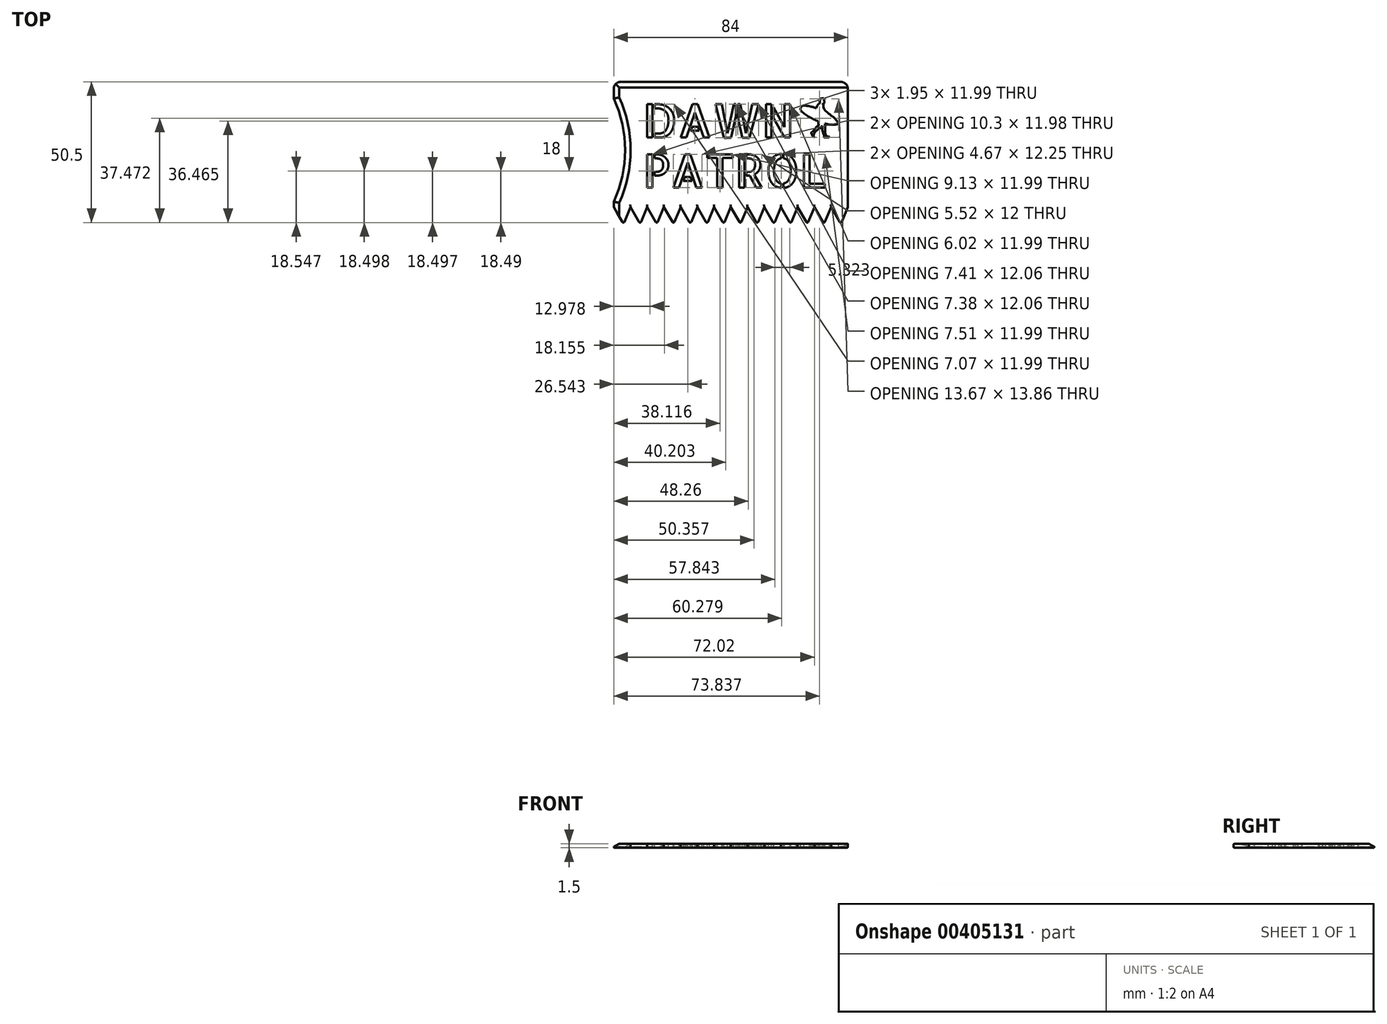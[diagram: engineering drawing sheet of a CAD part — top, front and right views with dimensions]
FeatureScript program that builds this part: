
annotation { "Feature Type Name" : "Feature", "Feature Type Description" : "" }
export const myFeature = defineFeature(function(context is Context, id is Id, definition is map)
    precondition{}
    {
        {
            assignVariable(context, id + "F0", {"name" : "t", "anyValue" : 1.5});
        }
        {
            var Q0;
            Q0=qCreatedBy(makeId("Top.planeOp"),FACE);
            var sketch = newSketch(context, id + "F1", { "sketchPlane" : qUnion([Q0])});
            skLineSegment(sketch, "E0.bottom", {"start": v(84, 51) * mm, "end": v(0, 51) * mm});
            skLineSegment(sketch, "E0.top", {"start": v(81.5, 0) * mm, "end": v(3.5, 0) * mm, "construction": true});
            skLineSegment(sketch, "E0.left", {"start": v(84, 51) * mm, "end": v(84, 6) * mm});
            skLineSegment(sketch, "E0.right", {"start": v(0, 51) * mm, "end": v(0, 6) * mm, "construction": true});
            skLineSegment(sketch, "E1", {"start": v(84, 6) * mm, "end": v(0, 6) * mm, "construction": true});
            skLineSegment(sketch, "E2", {"start": v(84, 6) * mm, "end": v(81.5, 0) * mm});
            skLineSegment(sketch, "E3", {"start": v(81.5, 0) * mm, "end": v(78, 6) * mm});
            skLineSegment(sketch, "E4.1.0.0", {"start": v(78, 6) * mm, "end": v(75.5, 0) * mm});
            skLineSegment(sketch, "E4.1.0.1", {"start": v(75.5, 0) * mm, "end": v(72, 6) * mm});
            skLineSegment(sketch, "E4.2.0.0", {"start": v(72, 6) * mm, "end": v(69.5, 0) * mm});
            skLineSegment(sketch, "E4.2.0.1", {"start": v(69.5, 0) * mm, "end": v(66, 6) * mm});
            skLineSegment(sketch, "E4.3.0.0", {"start": v(66, 6) * mm, "end": v(63.5, 0) * mm});
            skLineSegment(sketch, "E4.3.0.1", {"start": v(63.5, 0) * mm, "end": v(60, 6) * mm});
            skLineSegment(sketch, "E4.4.0.0", {"start": v(60, 6) * mm, "end": v(57.5, 0) * mm});
            skLineSegment(sketch, "E4.4.0.1", {"start": v(57.5, 0) * mm, "end": v(54, 6) * mm});
            skLineSegment(sketch, "E4.5.0.0", {"start": v(54, 6) * mm, "end": v(51.5, 0) * mm});
            skLineSegment(sketch, "E4.5.0.1", {"start": v(51.5, 0) * mm, "end": v(48, 6) * mm});
            skLineSegment(sketch, "E4.6.0.0", {"start": v(48, 6) * mm, "end": v(45.5, 0) * mm});
            skLineSegment(sketch, "E4.6.0.1", {"start": v(45.5, 0) * mm, "end": v(42, 6) * mm});
            skLineSegment(sketch, "E4.7.0.0", {"start": v(42, 6) * mm, "end": v(39.5, 0) * mm});
            skLineSegment(sketch, "E4.7.0.1", {"start": v(39.5, 0) * mm, "end": v(36, 6) * mm});
            skLineSegment(sketch, "E4.8.0.0", {"start": v(36, 6) * mm, "end": v(33.5, 0) * mm});
            skLineSegment(sketch, "E4.8.0.1", {"start": v(33.5, 0) * mm, "end": v(30, 6) * mm});
            skLineSegment(sketch, "E4.9.0.0", {"start": v(30, 6) * mm, "end": v(27.5, 0) * mm});
            skLineSegment(sketch, "E4.9.0.1", {"start": v(27.5, 0) * mm, "end": v(24, 6) * mm});
            skLineSegment(sketch, "E4.10.0.0", {"start": v(24, 6) * mm, "end": v(21.5, 0) * mm});
            skLineSegment(sketch, "E4.10.0.1", {"start": v(21.5, 0) * mm, "end": v(18, 6) * mm});
            skLineSegment(sketch, "E4.11.0.0", {"start": v(18, 6) * mm, "end": v(15.5, 0) * mm});
            skLineSegment(sketch, "E4.11.0.1", {"start": v(15.5, 0) * mm, "end": v(12, 6) * mm});
            skLineSegment(sketch, "E4.12.0.0", {"start": v(12, 6) * mm, "end": v(9.5, 0) * mm});
            skLineSegment(sketch, "E4.12.0.1", {"start": v(9.5, 0) * mm, "end": v(6, 6) * mm});
            skLineSegment(sketch, "E4.13.0.0", {"start": v(6, 6) * mm, "end": v(3.5, 0) * mm});
            skLineSegment(sketch, "E4.13.0.1", {"start": v(3.5, 0) * mm, "end": v(0, 6) * mm});
            skLineSegment(sketch, "E4.direction1", {"start": v(84, 6) * mm, "end": v(78, 6) * mm, "construction": true});
            skLineSegment(sketch, "E5", {"start": v(0, 6) * mm, "end": v(0, 8) * mm});
            skArc(sketch, "E6", {"start": v(0, 8) * mm, "mid": v(4.07, 26.5) * mm, "end": v(0, 45) * mm});
            skLineSegment(sketch, "E7", {"start": v(0, 45) * mm, "end": v(0, 51) * mm});
            skLineSegment(sketch, "E8", {"start": v(0, 6) * mm, "end": v(0, 0) * mm, "construction": true});
            skSolve(sketch);
        }
        {
            var Q0;
            Q0=qSketchRegion(id+"F1",true);
            extrude(context, id + "F2", {"entities" : qUnion([Q0]), "depth" : (getVariable(context, 't')) * mm});
        }
        {
            var Q0;
            Q0=makeQuery(id+"F2.opExtrude","CAP_EDGE",EDGE,{"disambiguationData":[OSD([sQuery(id+"F1.wireOp",EDGE,"E5")])],"isStart":false});
            var Q1;
            Q1=makeQuery(id+"F2.opExtrude","CAP_EDGE",EDGE,{"disambiguationData":[OSD([sQuery(id+"F1.wireOp",EDGE,"E6")])],"isStart":false});
            var Q2;
            Q2=makeQuery(id+"F2.opExtrude","CAP_EDGE",EDGE,{"disambiguationData":[OSD([sQuery(id+"F1.wireOp",EDGE,"E0.bottom")])],"isStart":false});
            var Q3;
            Q3=makeQuery(id+"F2.opExtrude","CAP_EDGE",EDGE,{"disambiguationData":[OSD([sQuery(id+"F1.wireOp",EDGE,"E7")])],"isStart":false});
            chamfer(context, id + "F3", {"entities" : qUnion([Q0, Q1, Q2, Q3]), "chamferType" : ChamferType.TWO_OFFSETS, "width1" : (getVariable(context, 't') * 2.2 / 3) * mm, "oppositeDirection" : false, "width2" : (getVariable(context, 't') * 4 / 3) * mm, "tangentPropagation" : true});
        }
        {
            var Q0;
            Q0=makeQuery(id+"F2.opExtrude","SWEPT_EDGE",EDGE,{"disambiguationData":[OSD([sQuery(id+"F1.wireOp",EDGE,"E0.bottom"),sQuery(id+"F1.wireOp",EDGE,"E7")])]});
            var Q1;
            Q1=makeQuery(id+"F2.opExtrude","SWEPT_EDGE",EDGE,{"disambiguationData":[OSD([sQuery(id+"F1.wireOp",EDGE,"E0.bottom"),sQuery(id+"F1.wireOp",EDGE,"E0.left")])]});
            fillet(context, id + "F4", {"entities" : qUnion([Q0, Q1]), "radius" : 2.5 * mm, "tangentPropagation" : true, "allowEdgeOverflow" : false});
        }
        {
            var Q0;
            Q0=makeQuery(id+"F2.opExtrude","CAP_FACE",FACE,{"disambiguationData":[OSD([sQuery(id+"F1.wireOp",EDGE,"E0.bottom"),sQuery(id+"F1.wireOp",EDGE,"E0.left"),sQuery(id+"F1.wireOp",EDGE,"E2"),sQuery(id+"F1.wireOp",EDGE,"E3"),sQuery(id+"F1.wireOp",EDGE,"E4.1.0.0"),sQuery(id+"F1.wireOp",EDGE,"E4.1.0.1"),sQuery(id+"F1.wireOp",EDGE,"E4.2.0.0"),sQuery(id+"F1.wireOp",EDGE,"E4.2.0.1"),sQuery(id+"F1.wireOp",EDGE,"E4.3.0.0"),sQuery(id+"F1.wireOp",EDGE,"E4.3.0.1"),sQuery(id+"F1.wireOp",EDGE,"E4.4.0.0"),sQuery(id+"F1.wireOp",EDGE,"E4.4.0.1"),sQuery(id+"F1.wireOp",EDGE,"E4.5.0.0"),sQuery(id+"F1.wireOp",EDGE,"E4.5.0.1"),sQuery(id+"F1.wireOp",EDGE,"E4.6.0.0"),sQuery(id+"F1.wireOp",EDGE,"E4.6.0.1"),sQuery(id+"F1.wireOp",EDGE,"E4.7.0.0"),sQuery(id+"F1.wireOp",EDGE,"E4.7.0.1"),sQuery(id+"F1.wireOp",EDGE,"E4.8.0.0"),sQuery(id+"F1.wireOp",EDGE,"E4.8.0.1"),sQuery(id+"F1.wireOp",EDGE,"E4.9.0.0"),sQuery(id+"F1.wireOp",EDGE,"E4.9.0.1"),sQuery(id+"F1.wireOp",EDGE,"E4.10.0.0"),sQuery(id+"F1.wireOp",EDGE,"E4.10.0.1"),sQuery(id+"F1.wireOp",EDGE,"E4.11.0.0"),sQuery(id+"F1.wireOp",EDGE,"E4.11.0.1"),sQuery(id+"F1.wireOp",EDGE,"E4.12.0.0"),sQuery(id+"F1.wireOp",EDGE,"E4.12.0.1"),sQuery(id+"F1.wireOp",EDGE,"E4.13.0.0"),sQuery(id+"F1.wireOp",EDGE,"E4.13.0.1"),sQuery(id+"F1.wireOp",EDGE,"E5"),sQuery(id+"F1.wireOp",EDGE,"E6"),sQuery(id+"F1.wireOp",EDGE,"E7")])],"isStart":false});
            var sketch = newSketch(context, id + "F5", { "sketchPlane" : qUnion([Q0])});
            skLineSegment(sketch, "E9.0", {"start": v(81.9, 6.42) * mm, "end": v(81.9, 46.9) * mm});
            skLineSegment(sketch, "E9.1", {"start": v(81.19, 4.7) * mm, "end": v(81.9, 6.42) * mm});
            skLineSegment(sketch, "E9.2", {"start": v(77.69, 10.7) * mm, "end": v(81.19, 4.7) * mm});
            skLineSegment(sketch, "E9.3", {"start": v(75.19, 4.7) * mm, "end": v(77.69, 10.7) * mm});
            skLineSegment(sketch, "E9.4", {"start": v(71.69, 10.7) * mm, "end": v(75.19, 4.7) * mm});
            skLineSegment(sketch, "E9.5", {"start": v(69.19, 4.7) * mm, "end": v(71.69, 10.7) * mm});
            skLineSegment(sketch, "E9.6", {"start": v(65.69, 10.7) * mm, "end": v(69.19, 4.7) * mm});
            skLineSegment(sketch, "E9.7", {"start": v(81.9, 46.9) * mm, "end": v(3.64, 46.9) * mm});
            skArc(sketch, "E9.8", {"start": v(3.64, 46.9) * mm, "mid": v(8.1, 29.09) * mm, "end": v(5.57, 10.9) * mm});
            skLineSegment(sketch, "E9.9", {"start": v(5.57, 10.9) * mm, "end": v(9.19, 4.7) * mm});
            skLineSegment(sketch, "E9.10", {"start": v(9.19, 4.7) * mm, "end": v(11.69, 10.7) * mm});
            skLineSegment(sketch, "E9.11", {"start": v(11.69, 10.7) * mm, "end": v(15.19, 4.7) * mm});
            skLineSegment(sketch, "E9.12", {"start": v(15.19, 4.7) * mm, "end": v(17.69, 10.7) * mm});
            skLineSegment(sketch, "E9.13", {"start": v(17.69, 10.7) * mm, "end": v(21.19, 4.7) * mm});
            skLineSegment(sketch, "E9.14", {"start": v(21.19, 4.7) * mm, "end": v(23.69, 10.7) * mm});
            skLineSegment(sketch, "E9.15", {"start": v(23.69, 10.7) * mm, "end": v(27.19, 4.7) * mm});
            skLineSegment(sketch, "E9.16", {"start": v(27.19, 4.7) * mm, "end": v(29.69, 10.7) * mm});
            skLineSegment(sketch, "E9.17", {"start": v(29.69, 10.7) * mm, "end": v(33.19, 4.7) * mm});
            skLineSegment(sketch, "E9.18", {"start": v(33.19, 4.7) * mm, "end": v(35.69, 10.7) * mm});
            skLineSegment(sketch, "E9.19", {"start": v(35.69, 10.7) * mm, "end": v(39.19, 4.7) * mm});
            skLineSegment(sketch, "E9.20", {"start": v(39.19, 4.7) * mm, "end": v(41.69, 10.7) * mm});
            skLineSegment(sketch, "E9.21", {"start": v(41.69, 10.7) * mm, "end": v(45.19, 4.7) * mm});
            skLineSegment(sketch, "E9.22", {"start": v(45.19, 4.7) * mm, "end": v(47.69, 10.7) * mm});
            skLineSegment(sketch, "E9.23", {"start": v(47.69, 10.7) * mm, "end": v(51.19, 4.7) * mm});
            skLineSegment(sketch, "E9.24", {"start": v(51.19, 4.7) * mm, "end": v(53.69, 10.7) * mm});
            skLineSegment(sketch, "E9.25", {"start": v(53.69, 10.7) * mm, "end": v(57.19, 4.7) * mm});
            skLineSegment(sketch, "E9.26", {"start": v(57.19, 4.7) * mm, "end": v(59.69, 10.7) * mm});
            skLineSegment(sketch, "E9.27", {"start": v(59.69, 10.7) * mm, "end": v(63.19, 4.7) * mm});
            skLineSegment(sketch, "E9.28", {"start": v(63.19, 4.7) * mm, "end": v(65.69, 10.7) * mm});
            skSolve(sketch);
        }
        {
            var Q0;
            Q0=makeQuery(id+"F2.opExtrude","CAP_FACE",FACE,{"disambiguationData":[OSD([sQuery(id+"F1.wireOp",EDGE,"E0.bottom"),sQuery(id+"F1.wireOp",EDGE,"E0.left"),sQuery(id+"F1.wireOp",EDGE,"E2"),sQuery(id+"F1.wireOp",EDGE,"E3"),sQuery(id+"F1.wireOp",EDGE,"E4.1.0.0"),sQuery(id+"F1.wireOp",EDGE,"E4.1.0.1"),sQuery(id+"F1.wireOp",EDGE,"E4.2.0.0"),sQuery(id+"F1.wireOp",EDGE,"E4.2.0.1"),sQuery(id+"F1.wireOp",EDGE,"E4.3.0.0"),sQuery(id+"F1.wireOp",EDGE,"E4.3.0.1"),sQuery(id+"F1.wireOp",EDGE,"E4.4.0.0"),sQuery(id+"F1.wireOp",EDGE,"E4.4.0.1"),sQuery(id+"F1.wireOp",EDGE,"E4.5.0.0"),sQuery(id+"F1.wireOp",EDGE,"E4.5.0.1"),sQuery(id+"F1.wireOp",EDGE,"E4.6.0.0"),sQuery(id+"F1.wireOp",EDGE,"E4.6.0.1"),sQuery(id+"F1.wireOp",EDGE,"E4.7.0.0"),sQuery(id+"F1.wireOp",EDGE,"E4.7.0.1"),sQuery(id+"F1.wireOp",EDGE,"E4.8.0.0"),sQuery(id+"F1.wireOp",EDGE,"E4.8.0.1"),sQuery(id+"F1.wireOp",EDGE,"E4.9.0.0"),sQuery(id+"F1.wireOp",EDGE,"E4.9.0.1"),sQuery(id+"F1.wireOp",EDGE,"E4.10.0.0"),sQuery(id+"F1.wireOp",EDGE,"E4.10.0.1"),sQuery(id+"F1.wireOp",EDGE,"E4.11.0.0"),sQuery(id+"F1.wireOp",EDGE,"E4.11.0.1"),sQuery(id+"F1.wireOp",EDGE,"E4.12.0.0"),sQuery(id+"F1.wireOp",EDGE,"E4.12.0.1"),sQuery(id+"F1.wireOp",EDGE,"E4.13.0.0"),sQuery(id+"F1.wireOp",EDGE,"E4.13.0.1"),sQuery(id+"F1.wireOp",EDGE,"E5"),sQuery(id+"F1.wireOp",EDGE,"E6"),sQuery(id+"F1.wireOp",EDGE,"E7")])],"isStart":true});
            var Q1;
            Q1=makeQuery(id+"F2.opExtrude","CAP_EDGE",EDGE,{"disambiguationData":[OSD([sQuery(id+"F1.wireOp",EDGE,"E4.13.0.1")])],"isStart":false});
            var Q2;
            Q2=makeQuery(id+"F2.opExtrude","CAP_EDGE",EDGE,{"disambiguationData":[OSD([sQuery(id+"F1.wireOp",EDGE,"E4.13.0.0")])],"isStart":false});
            var Q3;
            Q3=makeQuery(id+"F2.opExtrude","SWEPT_EDGE",EDGE,{"disambiguationData":[OSD([sQuery(id+"F1.wireOp",EDGE,"E4.13.0.0"),sQuery(id+"F1.wireOp",EDGE,"E4.13.0.1")])]});
            var Q4;
            Q4=makeQuery(id+"F2.opExtrude","CAP_EDGE",EDGE,{"disambiguationData":[OSD([sQuery(id+"F1.wireOp",EDGE,"E4.12.0.1")])],"isStart":false});
            var Q5;
            Q5=makeQuery(id+"F2.opExtrude","SWEPT_EDGE",EDGE,{"disambiguationData":[OSD([sQuery(id+"F1.wireOp",EDGE,"E4.12.0.0"),sQuery(id+"F1.wireOp",EDGE,"E4.12.0.1")])]});
            var Q6;
            Q6=makeQuery(id+"F2.opExtrude","CAP_EDGE",EDGE,{"disambiguationData":[OSD([sQuery(id+"F1.wireOp",EDGE,"E4.12.0.0")])],"isStart":false});
            var Q7;
            Q7=makeQuery(id+"F2.opExtrude","CAP_EDGE",EDGE,{"disambiguationData":[OSD([sQuery(id+"F1.wireOp",EDGE,"E4.11.0.1")])],"isStart":false});
            var Q8;
            Q8=makeQuery(id+"F2.opExtrude","SWEPT_EDGE",EDGE,{"disambiguationData":[OSD([sQuery(id+"F1.wireOp",EDGE,"E4.11.0.0"),sQuery(id+"F1.wireOp",EDGE,"E4.11.0.1")])]});
            var Q9;
            Q9=makeQuery(id+"F2.opExtrude","CAP_EDGE",EDGE,{"disambiguationData":[OSD([sQuery(id+"F1.wireOp",EDGE,"E4.11.0.0")])],"isStart":false});
            var Q10;
            Q10=makeQuery(id+"F2.opExtrude","CAP_EDGE",EDGE,{"disambiguationData":[OSD([sQuery(id+"F1.wireOp",EDGE,"E4.10.0.1")])],"isStart":false});
            var Q11;
            Q11=makeQuery(id+"F2.opExtrude","CAP_EDGE",EDGE,{"disambiguationData":[OSD([sQuery(id+"F1.wireOp",EDGE,"E4.10.0.0")])],"isStart":false});
            var Q12;
            Q12=makeQuery(id+"F2.opExtrude","CAP_EDGE",EDGE,{"disambiguationData":[OSD([sQuery(id+"F1.wireOp",EDGE,"E4.9.0.1")])],"isStart":false});
            var Q13;
            Q13=makeQuery(id+"F2.opExtrude","CAP_EDGE",EDGE,{"disambiguationData":[OSD([sQuery(id+"F1.wireOp",EDGE,"E4.9.0.0")])],"isStart":false});
            var Q14;
            Q14=makeQuery(id+"F2.opExtrude","CAP_EDGE",EDGE,{"disambiguationData":[OSD([sQuery(id+"F1.wireOp",EDGE,"E4.8.0.1")])],"isStart":false});
            var Q15;
            Q15=makeQuery(id+"F2.opExtrude","CAP_EDGE",EDGE,{"disambiguationData":[OSD([sQuery(id+"F1.wireOp",EDGE,"E4.8.0.0")])],"isStart":false});
            var Q16;
            Q16=makeQuery(id+"F2.opExtrude","CAP_EDGE",EDGE,{"disambiguationData":[OSD([sQuery(id+"F1.wireOp",EDGE,"E4.7.0.1")])],"isStart":false});
            var Q17;
            Q17=makeQuery(id+"F2.opExtrude","CAP_EDGE",EDGE,{"disambiguationData":[OSD([sQuery(id+"F1.wireOp",EDGE,"E4.7.0.0")])],"isStart":false});
            var Q18;
            Q18=makeQuery(id+"F2.opExtrude","CAP_EDGE",EDGE,{"disambiguationData":[OSD([sQuery(id+"F1.wireOp",EDGE,"E4.6.0.1")])],"isStart":false});
            var Q19;
            Q19=makeQuery(id+"F2.opExtrude","CAP_EDGE",EDGE,{"disambiguationData":[OSD([sQuery(id+"F1.wireOp",EDGE,"E4.6.0.0")])],"isStart":false});
            var Q20;
            Q20=makeQuery(id+"F2.opExtrude","CAP_EDGE",EDGE,{"disambiguationData":[OSD([sQuery(id+"F1.wireOp",EDGE,"E4.5.0.1")])],"isStart":false});
            var Q21;
            Q21=makeQuery(id+"F2.opExtrude","CAP_EDGE",EDGE,{"disambiguationData":[OSD([sQuery(id+"F1.wireOp",EDGE,"E4.5.0.0")])],"isStart":false});
            var Q22;
            Q22=makeQuery(id+"F2.opExtrude","CAP_EDGE",EDGE,{"disambiguationData":[OSD([sQuery(id+"F1.wireOp",EDGE,"E4.4.0.1")])],"isStart":false});
            var Q23;
            Q23=makeQuery(id+"F2.opExtrude","CAP_EDGE",EDGE,{"disambiguationData":[OSD([sQuery(id+"F1.wireOp",EDGE,"E4.4.0.0")])],"isStart":false});
            var Q24;
            Q24=makeQuery(id+"F2.opExtrude","CAP_EDGE",EDGE,{"disambiguationData":[OSD([sQuery(id+"F1.wireOp",EDGE,"E4.3.0.1")])],"isStart":false});
            var Q25;
            Q25=makeQuery(id+"F2.opExtrude","CAP_EDGE",EDGE,{"disambiguationData":[OSD([sQuery(id+"F1.wireOp",EDGE,"E4.3.0.0")])],"isStart":false});
            var Q26;
            Q26=makeQuery(id+"F2.opExtrude","CAP_EDGE",EDGE,{"disambiguationData":[OSD([sQuery(id+"F1.wireOp",EDGE,"E4.2.0.1")])],"isStart":false});
            var Q27;
            Q27=makeQuery(id+"F2.opExtrude","CAP_EDGE",EDGE,{"disambiguationData":[OSD([sQuery(id+"F1.wireOp",EDGE,"E4.2.0.0")])],"isStart":false});
            var Q28;
            Q28=makeQuery(id+"F2.opExtrude","CAP_EDGE",EDGE,{"disambiguationData":[OSD([sQuery(id+"F1.wireOp",EDGE,"E4.1.0.1")])],"isStart":false});
            var Q29;
            Q29=makeQuery(id+"F2.opExtrude","CAP_EDGE",EDGE,{"disambiguationData":[OSD([sQuery(id+"F1.wireOp",EDGE,"E4.1.0.0")])],"isStart":false});
            var Q30;
            Q30=makeQuery(id+"F2.opExtrude","CAP_EDGE",EDGE,{"disambiguationData":[OSD([sQuery(id+"F1.wireOp",EDGE,"E3")])],"isStart":false});
            var Q31;
            Q31=makeQuery(id+"F2.opExtrude","SWEPT_EDGE",EDGE,{"disambiguationData":[OSD([sQuery(id+"F1.wireOp",EDGE,"E2"),sQuery(id+"F1.wireOp",EDGE,"E3")])]});
            var Q32;
            Q32=makeQuery(id+"F2.opExtrude","CAP_EDGE",EDGE,{"disambiguationData":[OSD([sQuery(id+"F1.wireOp",EDGE,"E2")])],"isStart":false});
            var Q33;
            Q33=makeQuery(id+"F2.opExtrude","SWEPT_EDGE",EDGE,{"disambiguationData":[OSD([sQuery(id+"F1.wireOp",EDGE,"E4.1.0.0"),sQuery(id+"F1.wireOp",EDGE,"E4.1.0.1")])]});
            var Q34;
            Q34=makeQuery(id+"F2.opExtrude","SWEPT_EDGE",EDGE,{"disambiguationData":[OSD([sQuery(id+"F1.wireOp",EDGE,"E4.2.0.0"),sQuery(id+"F1.wireOp",EDGE,"E4.2.0.1")])]});
            var Q35;
            Q35=makeQuery(id+"F2.opExtrude","SWEPT_EDGE",EDGE,{"disambiguationData":[OSD([sQuery(id+"F1.wireOp",EDGE,"E4.3.0.0"),sQuery(id+"F1.wireOp",EDGE,"E4.3.0.1")])]});
            var Q36;
            Q36=makeQuery(id+"F2.opExtrude","SWEPT_EDGE",EDGE,{"disambiguationData":[OSD([sQuery(id+"F1.wireOp",EDGE,"E4.4.0.0"),sQuery(id+"F1.wireOp",EDGE,"E4.4.0.1")])]});
            var Q37;
            Q37=makeQuery(id+"F2.opExtrude","SWEPT_EDGE",EDGE,{"disambiguationData":[OSD([sQuery(id+"F1.wireOp",EDGE,"E4.5.0.0"),sQuery(id+"F1.wireOp",EDGE,"E4.5.0.1")])]});
            var Q38;
            Q38=makeQuery(id+"F2.opExtrude","SWEPT_EDGE",EDGE,{"disambiguationData":[OSD([sQuery(id+"F1.wireOp",EDGE,"E4.6.0.0"),sQuery(id+"F1.wireOp",EDGE,"E4.6.0.1")])]});
            var Q39;
            Q39=makeQuery(id+"F2.opExtrude","SWEPT_EDGE",EDGE,{"disambiguationData":[OSD([sQuery(id+"F1.wireOp",EDGE,"E4.7.0.0"),sQuery(id+"F1.wireOp",EDGE,"E4.7.0.1")])]});
            var Q40;
            Q40=makeQuery(id+"F2.opExtrude","SWEPT_EDGE",EDGE,{"disambiguationData":[OSD([sQuery(id+"F1.wireOp",EDGE,"E4.8.0.0"),sQuery(id+"F1.wireOp",EDGE,"E4.8.0.1")])]});
            var Q41;
            Q41=makeQuery(id+"F2.opExtrude","SWEPT_EDGE",EDGE,{"disambiguationData":[OSD([sQuery(id+"F1.wireOp",EDGE,"E4.9.0.0"),sQuery(id+"F1.wireOp",EDGE,"E4.9.0.1")])]});
            var Q42;
            Q42=makeQuery(id+"F2.opExtrude","SWEPT_EDGE",EDGE,{"disambiguationData":[OSD([sQuery(id+"F1.wireOp",EDGE,"E4.10.0.0"),sQuery(id+"F1.wireOp",EDGE,"E4.10.0.1")])]});
            fillet(context, id + "F6", {"entities" : qUnion([Q0, Q1, Q2, Q3, Q4, Q5, Q6, Q7, Q8, Q9, Q10, Q11, Q12, Q13, Q14, Q15, Q16, Q17, Q18, Q19, Q20, Q21, Q22, Q23, Q24, Q25, Q26, Q27, Q28, Q29, Q30, Q31, Q32, Q33, Q34, Q35, Q36, Q37, Q38, Q39, Q40, Q41, Q42]), "radius" : .4 * mm, "tangentPropagation" : true, "allowEdgeOverflow" : false});
        }
        {
            var Q0;
            Q0=makeQuery(id+"F2.opExtrude","CAP_FACE",FACE,{"disambiguationData":[OSD([sQuery(id+"F1.wireOp",EDGE,"E0.bottom"),sQuery(id+"F1.wireOp",EDGE,"E0.left"),sQuery(id+"F1.wireOp",EDGE,"E2"),sQuery(id+"F1.wireOp",EDGE,"E3"),sQuery(id+"F1.wireOp",EDGE,"E4.1.0.0"),sQuery(id+"F1.wireOp",EDGE,"E4.1.0.1"),sQuery(id+"F1.wireOp",EDGE,"E4.2.0.0"),sQuery(id+"F1.wireOp",EDGE,"E4.2.0.1"),sQuery(id+"F1.wireOp",EDGE,"E4.3.0.0"),sQuery(id+"F1.wireOp",EDGE,"E4.3.0.1"),sQuery(id+"F1.wireOp",EDGE,"E4.4.0.0"),sQuery(id+"F1.wireOp",EDGE,"E4.4.0.1"),sQuery(id+"F1.wireOp",EDGE,"E4.5.0.0"),sQuery(id+"F1.wireOp",EDGE,"E4.5.0.1"),sQuery(id+"F1.wireOp",EDGE,"E4.6.0.0"),sQuery(id+"F1.wireOp",EDGE,"E4.6.0.1"),sQuery(id+"F1.wireOp",EDGE,"E4.7.0.0"),sQuery(id+"F1.wireOp",EDGE,"E4.7.0.1"),sQuery(id+"F1.wireOp",EDGE,"E4.8.0.0"),sQuery(id+"F1.wireOp",EDGE,"E4.8.0.1"),sQuery(id+"F1.wireOp",EDGE,"E4.9.0.0"),sQuery(id+"F1.wireOp",EDGE,"E4.9.0.1"),sQuery(id+"F1.wireOp",EDGE,"E4.10.0.0"),sQuery(id+"F1.wireOp",EDGE,"E4.10.0.1"),sQuery(id+"F1.wireOp",EDGE,"E4.11.0.0"),sQuery(id+"F1.wireOp",EDGE,"E4.11.0.1"),sQuery(id+"F1.wireOp",EDGE,"E4.12.0.0"),sQuery(id+"F1.wireOp",EDGE,"E4.12.0.1"),sQuery(id+"F1.wireOp",EDGE,"E4.13.0.0"),sQuery(id+"F1.wireOp",EDGE,"E4.13.0.1"),sQuery(id+"F1.wireOp",EDGE,"E5"),sQuery(id+"F1.wireOp",EDGE,"E6"),sQuery(id+"F1.wireOp",EDGE,"E7")])],"isStart":false});
            var sketch = newSketch(context, id + "F7", { "sketchPlane" : qUnion([Q0])});
            skText(sketch, "E10", { "text": "PATROL", "fontName": "AllertaStencil-Regular.ttf"});
            skText(sketch, "E11", { "text": "DAWN", "fontName": "AllertaStencil-Regular.ttf"});
            const initialGuessF7  = {"E10": [0.01052, 0.013, 1, 0, 0.012], "E11": [0.01044, 0.031, 1, 0, 0.012]};
            skSetInitialGuess(sketch, initialGuessF7);
            skSolve(sketch);
        }
        {
            var Q0;
            Q0=qSketchRegion(id+"F7",true);
            extrude(context, id + "F8", {"entities" : qUnion([Q0]), "operationType" : NewBodyOperationType.REMOVE, "endBound" : BoundingType.THROUGH_ALL, "oppositeDirection" : true, "depth" : 25 * mm});
        }
        {
            var Q0;
            Q0=makeQuery(id+"F2.opExtrude","CAP_FACE",FACE,{"disambiguationData":[OSD([sQuery(id+"F1.wireOp",EDGE,"E0.bottom"),sQuery(id+"F1.wireOp",EDGE,"E0.left"),sQuery(id+"F1.wireOp",EDGE,"E2"),sQuery(id+"F1.wireOp",EDGE,"E3"),sQuery(id+"F1.wireOp",EDGE,"E4.1.0.0"),sQuery(id+"F1.wireOp",EDGE,"E4.1.0.1"),sQuery(id+"F1.wireOp",EDGE,"E4.2.0.0"),sQuery(id+"F1.wireOp",EDGE,"E4.2.0.1"),sQuery(id+"F1.wireOp",EDGE,"E4.3.0.0"),sQuery(id+"F1.wireOp",EDGE,"E4.3.0.1"),sQuery(id+"F1.wireOp",EDGE,"E4.4.0.0"),sQuery(id+"F1.wireOp",EDGE,"E4.4.0.1"),sQuery(id+"F1.wireOp",EDGE,"E4.5.0.0"),sQuery(id+"F1.wireOp",EDGE,"E4.5.0.1"),sQuery(id+"F1.wireOp",EDGE,"E4.6.0.0"),sQuery(id+"F1.wireOp",EDGE,"E4.6.0.1"),sQuery(id+"F1.wireOp",EDGE,"E4.7.0.0"),sQuery(id+"F1.wireOp",EDGE,"E4.7.0.1"),sQuery(id+"F1.wireOp",EDGE,"E4.8.0.0"),sQuery(id+"F1.wireOp",EDGE,"E4.8.0.1"),sQuery(id+"F1.wireOp",EDGE,"E4.9.0.0"),sQuery(id+"F1.wireOp",EDGE,"E4.9.0.1"),sQuery(id+"F1.wireOp",EDGE,"E4.10.0.0"),sQuery(id+"F1.wireOp",EDGE,"E4.10.0.1"),sQuery(id+"F1.wireOp",EDGE,"E4.11.0.0"),sQuery(id+"F1.wireOp",EDGE,"E4.11.0.1"),sQuery(id+"F1.wireOp",EDGE,"E4.12.0.0"),sQuery(id+"F1.wireOp",EDGE,"E4.12.0.1"),sQuery(id+"F1.wireOp",EDGE,"E4.13.0.0"),sQuery(id+"F1.wireOp",EDGE,"E4.13.0.1"),sQuery(id+"F1.wireOp",EDGE,"E5"),sQuery(id+"F1.wireOp",EDGE,"E6"),sQuery(id+"F1.wireOp",EDGE,"E7")])],"isStart":false});
            var sketch = newSketch(context, id + "F9", { "sketchPlane" : qUnion([Q0])});
            skLineSegment(sketch, "E12", {"start": v(66.95, 41.84) * mm, "end": v(80.97, 35.81) * mm, "construction": true});
            skFitSpline(sketch, "E13", {"points": [v(73.4, 36.87) * mm, v(70.8, 38.04) * mm, v(68.82, 39.24) * mm, v(67.19, 40.67) * mm, v(67, 41.22) * mm, v(67.13, 41.76) * mm], "startDerivative": vector(-8.18, 3.62) * mm, "endDerivative": vector(1.44, 4.42) * mm});
            skFitSpline(sketch, "E14", {"points": [v(74.41, 40.85) * mm, v(72.35, 41.67) * mm, v(70.12, 42.27) * mm, v(67.96, 42.47) * mm, v(67.44, 42.23) * mm, v(67.13, 41.76) * mm], "startDerivative": vector(-8.26, 3.44) * mm, "endDerivative": vector(-2.21, -4.08) * mm});
            skFitSpline(sketch, "E15", {"points": [v(73.4, 36.87) * mm, v(73.4, 36.1) * mm, v(73.57, 35.54) * mm, v(73.58, 35.27) * mm, v(73.43, 35.13) * mm, v(72.87, 34.87) * mm, v(72.4, 34.35) * mm, v(71.97, 33.73) * mm, v(71.61, 33.29) * mm, v(71.4, 33.12) * mm, v(71.1, 33) * mm, v(70.89, 32.9) * mm, v(70.83, 32.74) * mm, v(70.94, 32.4) * mm, v(71.1, 32.24) * mm, v(71.23, 32.12) * mm, v(71.27, 31.92) * mm, v(71.3, 31.52) * mm, v(71.46, 31.31) * mm, v(71.67, 31.2) * mm, v(71.95, 31.15) * mm, v(72, 31.18) * mm, v(72, 31.22) * mm, v(71.98, 31.3) * mm, v(71.86, 31.39) * mm, v(71.75, 31.5) * mm, v(71.73, 31.78) * mm, v(71.76, 32.1) * mm, v(71.8, 32.32) * mm, v(71.87, 32.48) * mm, v(72.07, 32.78) * mm, v(72.6, 33.3) * mm, v(73.2, 33.79) * mm, v(73.8, 34.23) * mm, v(74.35, 34.55) * mm, v(74.58, 34.75) * mm, v(74.67, 34.97) * mm, v(74.71, 35.17) * mm, v(74.77, 35.2) * mm, v(74.8, 35.2) * mm], "startDerivative": vector(-1.7, -19.21) * mm, "endDerivative": vector(3.01, -1.59) * mm});
            skFitSpline(sketch, "E16", {"points": [v(72.67, 41.55) * mm, v(72.93, 42.2) * mm, v(73.19, 42.72) * mm, v(73.47, 43.01) * mm, v(73.77, 43.26) * mm, v(73.98, 43.44) * mm, v(74.04, 43.56) * mm, v(73.93, 43.82) * mm, v(73.83, 44.16) * mm, v(73.88, 44.56) * mm, v(74.04, 44.88) * mm, v(74.58, 45.2) * mm, v(75.03, 45.12) * mm, v(75.35, 44.99) * mm, v(75.57, 44.76) * mm, v(75.55, 44.54) * mm, v(75.49, 44.42) * mm, v(75.55, 44.3) * mm, v(75.58, 44.15) * mm, v(75.53, 44.07) * mm, v(75.52, 44) * mm, v(75.6, 43.9) * mm, v(75.68, 43.78) * mm, v(75.68, 43.7) * mm, v(75.64, 43.64) * mm, v(75.52, 43.66) * mm, v(75.5, 43.6) * mm, v(75.5, 43.5) * mm, v(75.48, 43.43) * mm, v(75.43, 43.37) * mm, v(75.44, 43.28) * mm, v(75.47, 43.19) * mm, v(75.45, 43.12) * mm, v(75.36, 43.09) * mm, v(75.27, 43.05) * mm, v(75.09, 43.06) * mm, v(75, 43.08) * mm, v(74.93, 43.03) * mm, v(74.99, 42.93) * mm, v(75.15, 42.77) * mm, v(75.29, 42.44) * mm, v(75.3, 41.91) * mm, v(75.41, 41.43) * mm, v(75.64, 40.98) * mm, v(76.11, 40.51) * mm, v(76.5, 40.15) * mm, v(76.93, 39.85) * mm, v(77.24, 39.52) * mm, v(77.5, 39.4) * mm, v(77.82, 39.27) * mm, v(77.93, 39.07) * mm, v(77.96, 38.96) * mm], "startDerivative": vector(7.84, 19.36) * mm, "endDerivative": vector(2.4, -8.81) * mm});
            skFitSpline(sketch, "E17", {"points": [v(75.73, 36.07) * mm, v(76.39, 35.89) * mm, v(77.35, 35.68) * mm, v(78.3, 35.58) * mm, v(79.13, 35.62) * mm, v(80.02, 35.74) * mm, v(80.65, 35.9) * mm, v(80.67, 35.94) * mm], "startDerivative": vector(4.26, -1.27) * mm, "endDerivative": vector(0.24, 0.98) * mm});
            skFitSpline(sketch, "E18.MirrorCS", {"points": [v(77.18, 39.44) * mm, v(77.77, 39.09) * mm, v(78.58, 38.53) * mm, v(79.3, 37.92) * mm, v(79.85, 37.29) * mm, v(80.37, 36.56) * mm, v(80.68, 35.99) * mm, v(80.67, 35.94) * mm], "startDerivative": vector(3.85, -2.22) * mm, "endDerivative": vector(-0.55, -0.85) * mm});
            skFitSpline(sketch, "E19", {"points": [v(75.73, 36.07) * mm, v(75.84, 35.6) * mm, v(75.9, 35.3) * mm, v(75.88, 34.86) * mm, v(75.84, 34.23) * mm, v(75.85, 33.54) * mm, v(75.9, 32.74) * mm, v(76.03, 32.08) * mm, v(76.2, 31.77) * mm, v(76.47, 31.57) * mm, v(76.72, 31.41) * mm, v(77.02, 31.34) * mm, v(77.25, 31.32) * mm, v(77.35, 31.3) * mm, v(77.35, 31.22) * mm, v(77.3, 31.14) * mm, v(77.19, 31.09) * mm, v(77.02, 31.05) * mm, v(76.72, 31.04) * mm, v(76.27, 31.04) * mm, v(75.96, 31.06) * mm, v(75.71, 31.05) * mm, v(75.55, 31.06) * mm, v(75.46, 31.1) * mm, v(75.41, 31.23) * mm, v(75.42, 31.4) * mm, v(75.49, 31.58) * mm, v(75.5, 31.76) * mm, v(75.37, 32.09) * mm, v(75.16, 32.66) * mm, v(74.97, 33.33) * mm, v(74.83, 33.98) * mm, v(74.88, 34.56) * mm, v(74.9, 34.97) * mm, v(74.88, 35.14) * mm, v(74.8, 35.2) * mm], "startDerivative": vector(2.94, -13.83) * mm, "endDerivative": vector(-5.6, 2.93) * mm});
            skSolve(sketch);
        }
        {
            var Q0;
            Q0=makeQuery(id+"F9.imprint","IMPRINT",FACE,{"disambiguationData":[TD([[makeQuery(id+"F9.imprint","IMPRINT",EDGE,{"derivedFrom":sQuery(id+"F9.wireOp",EDGE,"E13")}),-1.0]])]});
            var Q1;
            {var subQ0=sQuery(id+"F1.wireOp",EDGE,"E7");var subQ1=sQuery(id+"F1.wireOp",EDGE,"E6");var subQ2=sQuery(id+"F1.wireOp",EDGE,"E5");var subQ3=sQuery(id+"F1.wireOp",EDGE,"E4.13.0.1");var subQ4=sQuery(id+"F1.wireOp",EDGE,"E4.13.0.0");var subQ5=sQuery(id+"F1.wireOp",EDGE,"E4.12.0.1");var subQ6=sQuery(id+"F1.wireOp",EDGE,"E4.12.0.0");var subQ7=sQuery(id+"F1.wireOp",EDGE,"E4.11.0.1");var subQ8=sQuery(id+"F1.wireOp",EDGE,"E4.11.0.0");var subQ9=sQuery(id+"F1.wireOp",EDGE,"E4.10.0.1");var subQ10=sQuery(id+"F1.wireOp",EDGE,"E4.10.0.0");var subQ11=sQuery(id+"F1.wireOp",EDGE,"E4.9.0.1");var subQ12=sQuery(id+"F1.wireOp",EDGE,"E4.9.0.0");var subQ13=sQuery(id+"F1.wireOp",EDGE,"E4.8.0.1");var subQ14=sQuery(id+"F1.wireOp",EDGE,"E4.8.0.0");var subQ15=sQuery(id+"F1.wireOp",EDGE,"E4.7.0.1");var subQ16=sQuery(id+"F1.wireOp",EDGE,"E4.7.0.0");var subQ17=sQuery(id+"F1.wireOp",EDGE,"E4.6.0.1");var subQ18=sQuery(id+"F1.wireOp",EDGE,"E4.6.0.0");var subQ19=sQuery(id+"F1.wireOp",EDGE,"E4.5.0.1");var subQ20=sQuery(id+"F1.wireOp",EDGE,"E4.5.0.0");var subQ21=sQuery(id+"F1.wireOp",EDGE,"E4.4.0.1");var subQ22=sQuery(id+"F1.wireOp",EDGE,"E4.4.0.0");var subQ23=sQuery(id+"F1.wireOp",EDGE,"E4.3.0.1");var subQ24=sQuery(id+"F1.wireOp",EDGE,"E4.3.0.0");var subQ25=sQuery(id+"F1.wireOp",EDGE,"E4.2.0.1");var subQ26=sQuery(id+"F1.wireOp",EDGE,"E4.2.0.0");var subQ27=sQuery(id+"F1.wireOp",EDGE,"E4.1.0.1");var subQ28=sQuery(id+"F1.wireOp",EDGE,"E4.1.0.0");var subQ29=sQuery(id+"F1.wireOp",EDGE,"E3");var subQ30=sQuery(id+"F1.wireOp",EDGE,"E2");var subQ31=sQuery(id+"F1.wireOp",EDGE,"E0.left");var subQ32=sQuery(id+"F1.wireOp",EDGE,"E0.bottom");Q1=makeQuery(id+"FXmY1YLn0CrPCvh_1.boolean.opBoolean","MERGE",FACE,{"derivedFrom":[makeQuery(id+"F2.opExtrude","CAP_FACE",FACE,{"disambiguationData":[OSD([subQ32,subQ31,subQ30,subQ29,subQ28,subQ27,subQ26,subQ25,subQ24,subQ23,subQ22,subQ21,subQ20,subQ19,subQ18,subQ17,subQ16,subQ15,subQ14,subQ13,subQ12,subQ11,subQ10,subQ9,subQ8,subQ7,subQ6,subQ5,subQ4,subQ3,subQ2,subQ1,subQ0])],"isStart":false}),makeQuery(id+"FXmY1YLn0CrPCvh_1.opExtrude","CAP_FACE",FACE,{"disambiguationData":[OSD([subQ32,subQ31,subQ30,subQ29,subQ28,subQ27,subQ26,subQ25,subQ24,subQ23,subQ22,subQ21,subQ20,subQ19,subQ18,subQ17,subQ16,subQ15,subQ14,subQ13,subQ12,subQ11,subQ10,subQ9,subQ8,subQ7,subQ6,subQ5,subQ4,subQ3,subQ2,subQ1,subQ0])],"isStart":false})]});}
            extrude(context, id + "F10", {"entities" : qUnion([Q0]), "operationType" : NewBodyOperationType.REMOVE, "endBound" : BoundingType.THROUGH_ALL, "oppositeDirection" : true, "endBoundEntityFace" : qUnion([Q1]), "depth" : 25 * mm});
        }
    });
